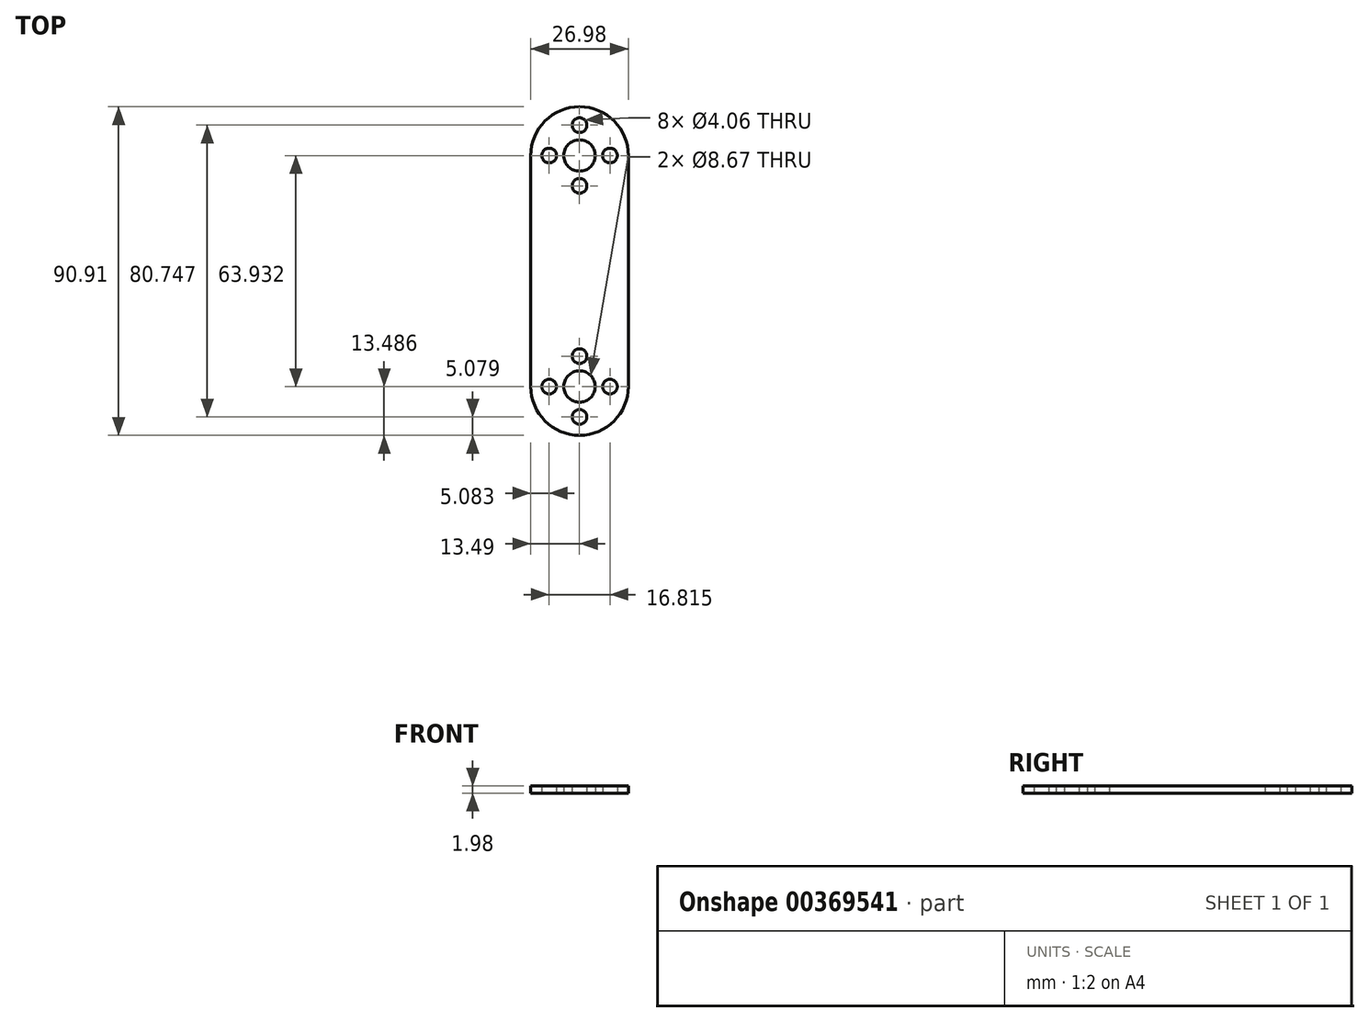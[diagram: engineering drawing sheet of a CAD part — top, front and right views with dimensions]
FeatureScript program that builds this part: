
annotation { "Feature Type Name" : "Feature", "Feature Type Description" : "" }
export const myFeature = defineFeature(function(context is Context, id is Id, definition is map)
    precondition{}
    {
        {
            var Q0;
            Q0=qCreatedBy(makeId("Top.planeOp"),FACE);
            var sketch = newSketch(context, id + "F0", { "sketchPlane" : qUnion([Q0])});
            skArc(sketch, "E0", {"start": v(13.49, 26.97) * mm, "mid": v(0, 40.46) * mm, "end": v(-13.49, 26.97) * mm});
            skArc(sketch, "E1", {"start": v(-13.49, -36.96) * mm, "mid": v(0, -50.45) * mm, "end": v(13.49, -36.96) * mm});
            skLineSegment(sketch, "E2", {"start": v(-13.49, 26.97) * mm, "end": v(-13.49, -36.96) * mm});
            skLineSegment(sketch, "E3", {"start": v(13.49, 26.97) * mm, "end": v(13.49, -36.96) * mm});
            skPoint(sketch, "E4", {"position": v(0, 40.46) * mm});
            skPoint(sketch, "E5", {"position": v(0, -50.45) * mm});
            skCircle(sketch, "E6", {"center": v(0, 26.97) * mm, "radius": 4.34 * mm});
            skPoint(sketch, "E7", {"position": v(0, 35.38) * mm});
            skPoint(sketch, "E8", {"position": v(-8.4, 26.97) * mm});
            skPoint(sketch, "E9", {"position": v(8.4, 26.97) * mm});
            skCircle(sketch, "E10", {"center": v(0, 35.38) * mm, "radius": 2.03 * mm});
            skCircle(sketch, "E11", {"center": v(-8.4, 26.97) * mm, "radius": 2.03 * mm});
            skCircle(sketch, "E12", {"center": v(8.4, 26.97) * mm, "radius": 2.03 * mm});
            skPoint(sketch, "E13", {"position": v(0, 18.56) * mm});
            skCircle(sketch, "E14", {"center": v(0, 18.56) * mm, "radius": 2.03 * mm});
            skCircle(sketch, "E15.MirrorC", {"center": v(0, -28.56) * mm, "radius": 2.03 * mm});
            skCircle(sketch, "E16.MirrorC", {"center": v(0, -36.96) * mm, "radius": 4.34 * mm});
            skCircle(sketch, "E17.MirrorC", {"center": v(-8.4, -36.96) * mm, "radius": 2.03 * mm});
            skCircle(sketch, "E18.MirrorC", {"center": v(0, -45.37) * mm, "radius": 2.03 * mm});
            skCircle(sketch, "E19.MirrorC", {"center": v(8.4, -36.96) * mm, "radius": 2.03 * mm});
            skPoint(sketch, "E20.end.orphan", {"position": v(13.49, -5) * mm});
            skPoint(sketch, "E20.start.orphan", {"position": v(-13.49, -5) * mm});
            skSolve(sketch);
        }
        {
            var Q0;
            Q0=makeQuery(id+"F0.imprint","IMPRINT",FACE,{"disambiguationData":[TD([[makeQuery(id+"F0.imprint","IMPRINT",EDGE,{"derivedFrom":sQuery(id+"F0.wireOp",EDGE,"E0")}),1.0]])]});
            var Q1;
            Q1 = qSketchRegion(id + "F0", true);
            extrude(context, id + "F1", {"entities" : qUnion([Q0, Q1]), "depth" : 1.98 * mm});
        }
    });
